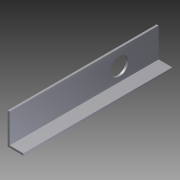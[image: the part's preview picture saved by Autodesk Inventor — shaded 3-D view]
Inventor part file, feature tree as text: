
AUTODESK INVENTOR PART (.ipt)
format: ipt  version: 2012 (Build 160160000, 160)  size: 86,528 bytes
history: native  units: in
note: dims shown in document units (in); Inventor stores cm internally (conversion verified against a paired STEP export)
features: extrude x2, sketch x2
ambient origin geometry x8: Origin, YZ Plane, XZ Plane, XY Plane, X Axis, Y Axis, Z Axis, Center Point
bodies: Solid1 (feature_tree)
feature tree (4):
  extrude  "Extrusion1"  Depth=1.0in
  extrude  "Extrusion2"  Depth=0.125in
  sketch  "Sketch1"  dims[d0=2.0in d1=1.0in]
  sketch  "Sketch2"  dims[d2=0.125in d3=0.125in d4=9.5in d5=0.0in d6=1.125in d7=2.5in d8=1.0in d9=4.0in d10=0.0in]
